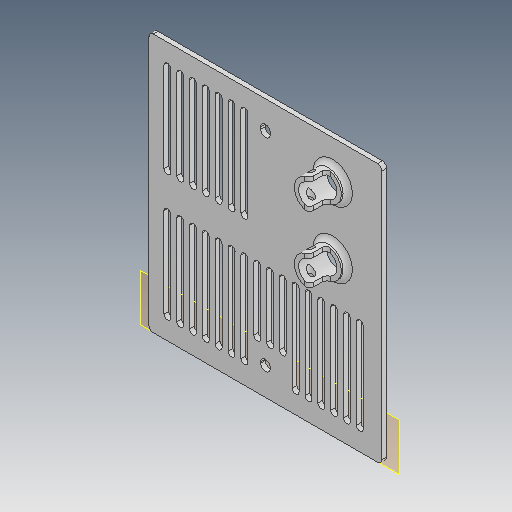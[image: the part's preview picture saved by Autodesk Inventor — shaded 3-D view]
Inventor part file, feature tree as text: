
AUTODESK INVENTOR PART (.ipt)
format: ipt  version: 2020 (Build 240168000, 168)  size: 401,920 bytes
history: native  units: mm
features: other x9, extrude x4, sketch x4, fillet x2
ambient origin geometry x8: Origin, YZ Plane, XZ Plane, XY Plane, X Axis, Y Axis, Z Axis, Center Point
bodies: Body1 (feature_tree)
feature tree (19):
  other  "Sólido1"
  other  "Plano de trabalho1"
  extrude  "Extrusão1"  Depth=0.5mm
  extrude  "Extrusão2"  Depth=1.0mm
  fillet  "Arredondamento1"  Radius=0.5mm
  extrude  "Extrusão3"  Depth=4.5mm
  extrude  "Extrusão4"  Depth=2.0mm
  fillet  "Arredondamento2"  Radius=10.0mm
  sketch  "Esboço1"  dims[d0=0.5mm d1=0.5mm]
  other  "Referência1"
  other  "Referência2"
  sketch  "Esboço2"  dims[d2=1.0mm d3=1.0mm d4=0.5mm]
  sketch  "Esboço3"  dims[d5=0.5mm d6=4.5mm]
  other  "Contorno projetado1"
  other  "Contorno projetado2"
  sketch  "Esboço4"  dims[d7=0.5mm d8=4.5mm d9=10.0mm d10=10.0mm d11=18.0mm d12=23.0mm d13=23.0mm d14=31.0mm d15=42.0mm d16=42.0mm d17=31.0mm d18=31.0mm d19=3.2mm d20=3.2mm d21=70.0mm d23=6.0mm d24=10.0mm d26=10.0mm d28=2.2mm d29=0.0mm d30=3.2mm d31=6.0mm d32=30.0mm d34=6.0mm d35=10.0mm d37=10.0mm d39=3.2mm d40=6.0mm d41=50.0mm d43=6.0mm d44=10.0mm d46=10.0mm d48=20.0mm d50=6.0mm d51=10.0mm d53=10.0mm d55=14.0mm d56=14.0mm d57=3.0mm d58=0.0mm d59=2.2mm d60=8.0mm d61=0.0mm d62=3.0mm d63=100.0mm d64=0.0mm d65=2.0mm]
  other  "Calorímetro.iam"
  other  "suporte_fechamento:2"
  other  "suporte_fechamento:3"
